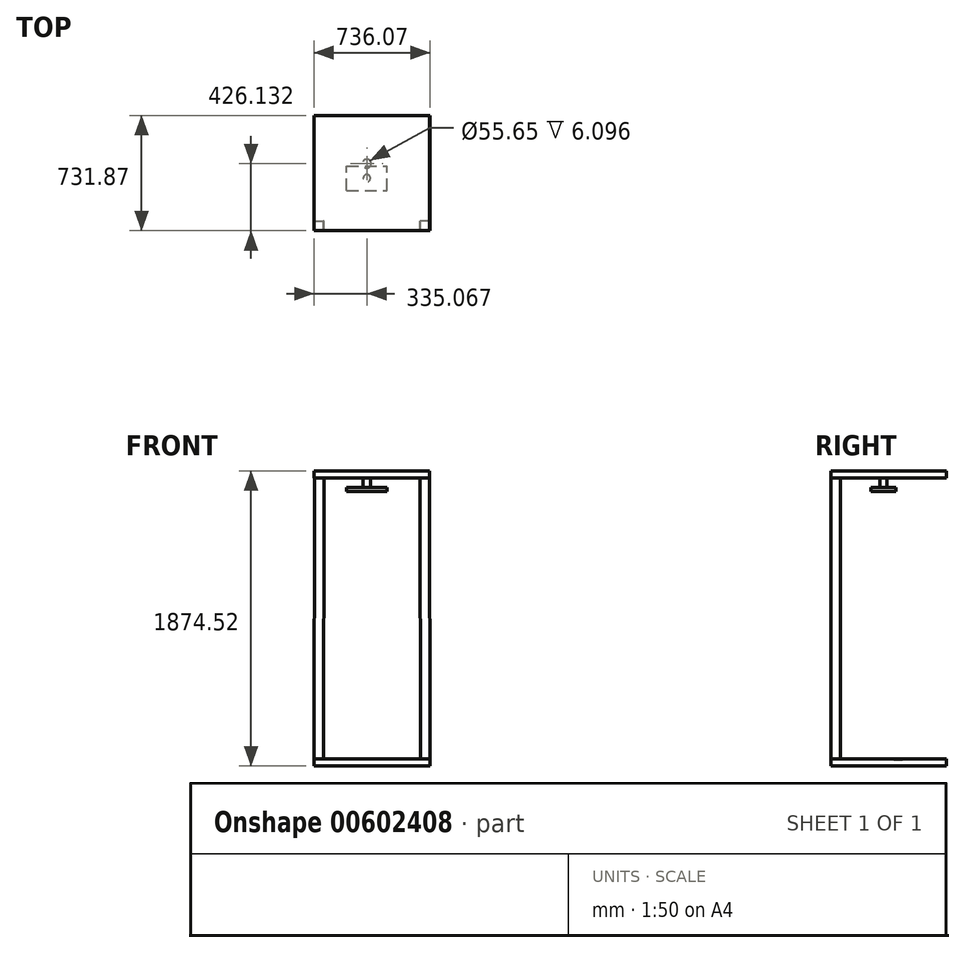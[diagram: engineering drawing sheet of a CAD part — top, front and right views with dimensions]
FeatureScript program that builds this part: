
annotation { "Feature Type Name" : "Feature", "Feature Type Description" : "" }
export const myFeature = defineFeature(function(context is Context, id is Id, definition is map)
    precondition{}
    {
        {
            var Q0;
            Q0=qCreatedBy(makeId("Top.planeOp"),FACE);
            var sketch = newSketch(context, id + "F0", { "sketchPlane" : qUnion([Q0])});
            skLineSegment(sketch, "E0.bottom", {"start": v(0, 0) * mm, "end": v(731.52, 0) * mm});
            skLineSegment(sketch, "E0.top", {"start": v(0, -731.52) * mm, "end": v(731.52, -731.52) * mm});
            skLineSegment(sketch, "E0.left", {"start": v(0, 0) * mm, "end": v(0, -731.52) * mm});
            skLineSegment(sketch, "E0.right", {"start": v(731.52, 0) * mm, "end": v(731.52, -731.52) * mm});
            skSolve(sketch);
        }
        {
            var Q0;
            Q0=makeQuery(id+"F0.imprint","IMPRINT",FACE,{"disambiguationData":[TD([[makeQuery(id+"F0.imprint","IMPRINT",EDGE,{"derivedFrom":sQuery(id+"F0.wireOp",EDGE,"E0.bottom")}),-1.0]])]});
            extrude(context, id + "F1", {"entities" : qUnion([Q0]), "depth" : 45.72 * mm, "offsetDistance" : 30.48 * mm});
        }
        {
            var Q0;
            Q0=qCreatedBy(makeId("Top.planeOp"),FACE);
            cPlane(context, id + "F2", {"entities" : qUnion([Q0]), "cplaneType" : CPlaneType.OFFSET, "offset" : 1828.8 * mm, "oppositeDirection" : true, "width" : 152.4 * mm, "height" : 152.4 * mm});
        }
        {
            var Q0;
            Q0=qCreatedBy(id+"F2.planeOp",FACE);
            var sketch = newSketch(context, id + "F3", { "sketchPlane" : qUnion([Q0])});
            skLineSegment(sketch, "E1.bottom", {"start": v(0, 0) * mm, "end": v(734.71, 0) * mm});
            skLineSegment(sketch, "E1.top", {"start": v(0, -731.87) * mm, "end": v(734.71, -731.87) * mm});
            skLineSegment(sketch, "E1.left", {"start": v(0, 0) * mm, "end": v(0, -731.87) * mm});
            skLineSegment(sketch, "E1.right", {"start": v(734.71, 0) * mm, "end": v(734.71, -731.87) * mm});
            skSolve(sketch);
        }
        {
            var Q0;
            Q0 = qSketchRegion(id + "F3", true);
            extrude(context, id + "F4", {"entities" : qUnion([Q0]), "depth" : 45.72 * mm, "offsetDistance" : 30.48 * mm});
        }
        {
            var Q0;
            Q0=makeQuery(id+"F1.opExtrude","CAP_FACE",FACE,{"disambiguationData":[OSD([sQuery(id+"F0.wireOp",EDGE,"E0.bottom"),sQuery(id+"F0.wireOp",EDGE,"E0.top"),sQuery(id+"F0.wireOp",EDGE,"E0.left"),sQuery(id+"F0.wireOp",EDGE,"E0.right")])],"isStart":true});
            var sketch = newSketch(context, id + "F5", { "sketchPlane" : qUnion([Q0])});
            skLineSegment(sketch, "E2.bottom", {"start": v(731.52, 731.52) * mm, "end": v(670.56, 731.52) * mm});
            skLineSegment(sketch, "E2.top", {"start": v(731.52, 670.56) * mm, "end": v(670.56, 670.56) * mm});
            skLineSegment(sketch, "E2.left", {"start": v(731.52, 731.52) * mm, "end": v(731.52, 670.56) * mm});
            skLineSegment(sketch, "E2.right", {"start": v(670.56, 731.52) * mm, "end": v(670.56, 670.56) * mm});
            skSolve(sketch);
        }
        {
            var Q0;
            Q0=makeQuery(id+"F4.opExtrude","CAP_FACE",FACE,{"disambiguationData":[OSD([sQuery(id+"F3.wireOp",EDGE,"E1.bottom"),sQuery(id+"F3.wireOp",EDGE,"E1.top"),sQuery(id+"F3.wireOp",EDGE,"E1.left"),sQuery(id+"F3.wireOp",EDGE,"E1.right")])],"isStart":false});
            var sketch = newSketch(context, id + "F6", { "sketchPlane" : qUnion([Q0])});
            skLineSegment(sketch, "E3.bottom", {"start": v(734.71, -731.87) * mm, "end": v(673.75, -731.87) * mm});
            skLineSegment(sketch, "E3.top", {"start": v(734.71, -670.91) * mm, "end": v(673.75, -670.91) * mm});
            skLineSegment(sketch, "E3.left", {"start": v(734.71, -731.87) * mm, "end": v(734.71, -670.91) * mm});
            skLineSegment(sketch, "E3.right", {"start": v(673.75, -731.87) * mm, "end": v(673.75, -670.91) * mm});
            skSolve(sketch);
        }
        {
            var Q0;
            Q0=makeQuery(id+"F5.imprint","IMPRINT",FACE,{"disambiguationData":[TD([[makeQuery(id+"F5.imprint","IMPRINT",EDGE,{"derivedFrom":sQuery(id+"F5.wireOp",EDGE,"E2.bottom")}),-1.0]])]});
            var Q1;
            Q1=makeQuery(id+"F6.imprint","IMPRINT",FACE,{"disambiguationData":[TD([[makeQuery(id+"F6.imprint","IMPRINT",EDGE,{"derivedFrom":sQuery(id+"F6.wireOp",EDGE,"E3.bottom")}),1.0]])]});
            loft(context, id + "F7", {"sheetProfilesArray" : [{ "sheetProfileEntities" : qUnion([Q0]) }, { "sheetProfileEntities" : qUnion([Q1]) }]});
        }
        {
            var Q0;
            Q0=makeQuery(id+"F7.opLoft","SWEPT_BODY",BODY,{"disambiguationData":[OSD([makeQuery(id+"F5.imprint","IMPRINT",FACE,{"disambiguationData":[TD([[makeQuery(id+"F5.imprint","IMPRINT",EDGE,{"derivedFrom":sQuery(id+"F5.wireOp",EDGE,"E2.bottom")}),-1.0]])]}),makeQuery(id+"F6.imprint","IMPRINT",FACE,{"disambiguationData":[TD([[makeQuery(id+"F6.imprint","IMPRINT",EDGE,{"derivedFrom":sQuery(id+"F6.wireOp",EDGE,"E3.bottom")}),1.0]])]})])]});
            var Q1;
            Q1=qCreatedBy(makeId("Right.planeOp"),FACE);
            mirror(context, id + "F8", {"entities" : qUnion([Q0]), "mirrorPlane" : qUnion([Q1])});
        }
        {
            var Q0;
            Q0=makeQuery(id+"F8.opPattern","COPY",BODY,{"derivedFrom":makeQuery(id+"F7.opLoft","SWEPT_BODY",BODY,{"disambiguationData":[OSD([makeQuery(id+"F5.imprint","IMPRINT",FACE,{"disambiguationData":[TD([[makeQuery(id+"F5.imprint","IMPRINT",EDGE,{"derivedFrom":sQuery(id+"F5.wireOp",EDGE,"E2.bottom")}),-1.0]])]}),makeQuery(id+"F6.imprint","IMPRINT",FACE,{"disambiguationData":[TD([[makeQuery(id+"F6.imprint","IMPRINT",EDGE,{"derivedFrom":sQuery(id+"F6.wireOp",EDGE,"E3.bottom")}),1.0]])]})])]}),"instanceName":"1"});
            deleteBodies(context, id + "F9", {"entities" : qUnion([Q0])});
        }
        {
            var Q0;
            Q0=qCreatedBy(makeId("Right.planeOp"),FACE);
            cPlane(context, id + "F10", {"entities" : qUnion([Q0]), "cplaneType" : CPlaneType.OFFSET, "offset" : 366.67 * mm, "width" : 152.4 * mm, "height" : 152.4 * mm});
        }
        {
            var Q0;
            Q0=makeQuery(id+"F7.opLoft","SWEPT_BODY",BODY,{"disambiguationData":[OSD([makeQuery(id+"F5.imprint","IMPRINT",FACE,{"disambiguationData":[TD([[makeQuery(id+"F5.imprint","IMPRINT",EDGE,{"derivedFrom":sQuery(id+"F5.wireOp",EDGE,"E2.bottom")}),-1.0]])]}),makeQuery(id+"F6.imprint","IMPRINT",FACE,{"disambiguationData":[TD([[makeQuery(id+"F6.imprint","IMPRINT",EDGE,{"derivedFrom":sQuery(id+"F6.wireOp",EDGE,"E3.bottom")}),1.0]])]})])]});
            var Q1;
            Q1=qCreatedBy(id+"F10.planeOp",FACE);
            mirror(context, id + "F11", {"entities" : qUnion([Q0]), "mirrorPlane" : qUnion([Q1])});
        }
        {
            var Q0;
            Q0=makeQuery(id+"F4.opExtrude","CAP_FACE",FACE,{"disambiguationData":[OSD([sQuery(id+"F3.wireOp",EDGE,"E1.bottom"),sQuery(id+"F3.wireOp",EDGE,"E1.top"),sQuery(id+"F3.wireOp",EDGE,"E1.left"),sQuery(id+"F3.wireOp",EDGE,"E1.right")])],"isStart":false});
            var sketch = newSketch(context, id + "F12", { "sketchPlane" : qUnion([Q0])});
            skCircle(sketch, "E4", {"center": v(333.7, -305.74) * mm, "radius": 27.82 * mm});
            skSolve(sketch);
        }
        {
            var Q0;
            Q0=makeQuery(id+"F12.imprint","IMPRINT",FACE,{"disambiguationData":[TD([[makeQuery(id+"F12.imprint","IMPRINT",EDGE,{"derivedFrom":sQuery(id+"F12.wireOp",EDGE,"E4")}),1.0]])]});
            extrude(context, id + "F13", {"entities" : qUnion([Q0]), "operationType" : NewBodyOperationType.REMOVE, "oppositeDirection" : true, "depth" : 6.1 * mm, "offsetDistance" : 30.48 * mm});
        }
        {
            var Q0;
            Q0=makeQuery(id+"F1.opExtrude","CAP_FACE",FACE,{"disambiguationData":[OSD([sQuery(id+"F0.wireOp",EDGE,"E0.bottom"),sQuery(id+"F0.wireOp",EDGE,"E0.top"),sQuery(id+"F0.wireOp",EDGE,"E0.left"),sQuery(id+"F0.wireOp",EDGE,"E0.right")])],"isStart":true});
            var sketch = newSketch(context, id + "F14", { "sketchPlane" : qUnion([Q0])});
            skCircle(sketch, "E5", {"center": v(333.92, 398.33) * mm, "radius": 22.77 * mm});
            skSolve(sketch);
        }
        {
            var Q0;
            Q0 = qSketchRegion(id + "F14", true);
            extrude(context, id + "F15", {"entities" : qUnion([Q0]), "operationType" : NewBodyOperationType.ADD, "depth" : 60.96 * mm, "offsetDistance" : 30.48 * mm});
        }
        {
            var Q0;
            Q0=makeQuery(id+"F15.opExtrude","CAP_FACE",FACE,{"disambiguationData":[OSD([sQuery(id+"F14.wireOp",EDGE,"E5")])],"isStart":false});
            var sketch = newSketch(context, id + "F16", { "sketchPlane" : qUnion([Q0])});
            skLineSegment(sketch, "E6.bottom", {"start": v(205.9, 476.56) * mm, "end": v(461.95, 476.56) * mm});
            skLineSegment(sketch, "E6.top", {"start": v(205.9, 320.1) * mm, "end": v(461.95, 320.1) * mm});
            skLineSegment(sketch, "E6.left", {"start": v(205.9, 476.56) * mm, "end": v(205.9, 320.1) * mm});
            skLineSegment(sketch, "E6.right", {"start": v(461.95, 476.56) * mm, "end": v(461.95, 320.1) * mm});
            skPoint(sketch, "E6.middle", {"position": v(333.92, 398.33) * mm});
            skSolve(sketch);
        }
        {
            var Q0;
            Q0=makeQuery(id+"F16.imprint","IMPRINT",FACE,{"disambiguationData":[TD([[makeQuery(id+"F16.imprint","IMPRINT",EDGE,{"derivedFrom":sQuery(id+"F16.wireOp",EDGE,"E6.bottom")}),-1.0]])]});
            var Q1;
            Q1=makeQuery(id+"F16.imprint","IMPRINT",FACE,{"disambiguationData":[TD([[makeQuery(id+"F16.imprint","IMPRINT",EDGE,{"derivedFrom":makeQuery(id+"F15.opExtrude","CAP_EDGE",EDGE,{"disambiguationData":[OSD([sQuery(id+"F14.wireOp",EDGE,"E5")])],"isStart":false})}),1.0]])]});
            extrude(context, id + "F17", {"entities" : qUnion([Q0, Q1]), "operationType" : NewBodyOperationType.ADD, "depth" : 24.38 * mm, "offsetDistance" : 30.48 * mm});
        }
    });
